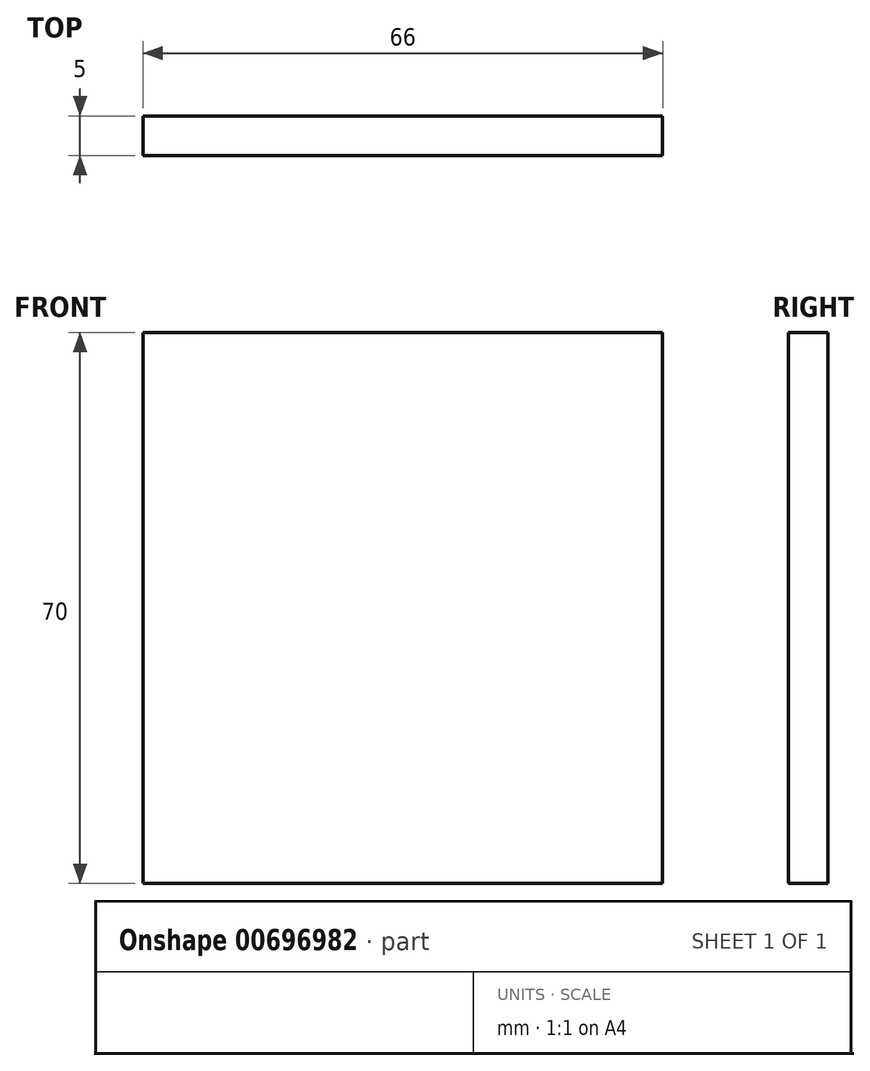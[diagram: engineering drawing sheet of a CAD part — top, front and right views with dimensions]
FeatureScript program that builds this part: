
annotation { "Feature Type Name" : "Feature", "Feature Type Description" : "" }
export const myFeature = defineFeature(function(context is Context, id is Id, definition is map)
    precondition{}
    {
        {
            var Q0;
            Q0=qCreatedBy(makeId("Front.planeOp"),FACE);
            var sketch = newSketch(context, id + "F0", { "sketchPlane" : qUnion([Q0])});
            skLineSegment(sketch, "E0.bottom", {"start": v(-620.22, 38.28) * mm, "end": v(-554.22, 38.28) * mm});
            skLineSegment(sketch, "E0.top", {"start": v(-620.22, -31.72) * mm, "end": v(-554.22, -31.72) * mm});
            skLineSegment(sketch, "E0.left", {"start": v(-620.22, 38.28) * mm, "end": v(-620.22, -31.72) * mm});
            skLineSegment(sketch, "E0.right", {"start": v(-554.22, 38.28) * mm, "end": v(-554.22, -31.72) * mm});
            skSolve(sketch);
        }
        {
            var Q0;
            Q0=makeQuery(id+"F0.imprint","IMPRINT",FACE,{"disambiguationData":[TD([[makeQuery(id+"F0.imprint","IMPRINT",EDGE,{"derivedFrom":sQuery(id+"F0.wireOp",EDGE,"E0.bottom")}),-1.0]])]});
            extrude(context, id + "F1", {"entities" : qUnion([Q0]), "depth" : 5 * mm, "offsetDistance" : 25 * mm});
        }
    });
